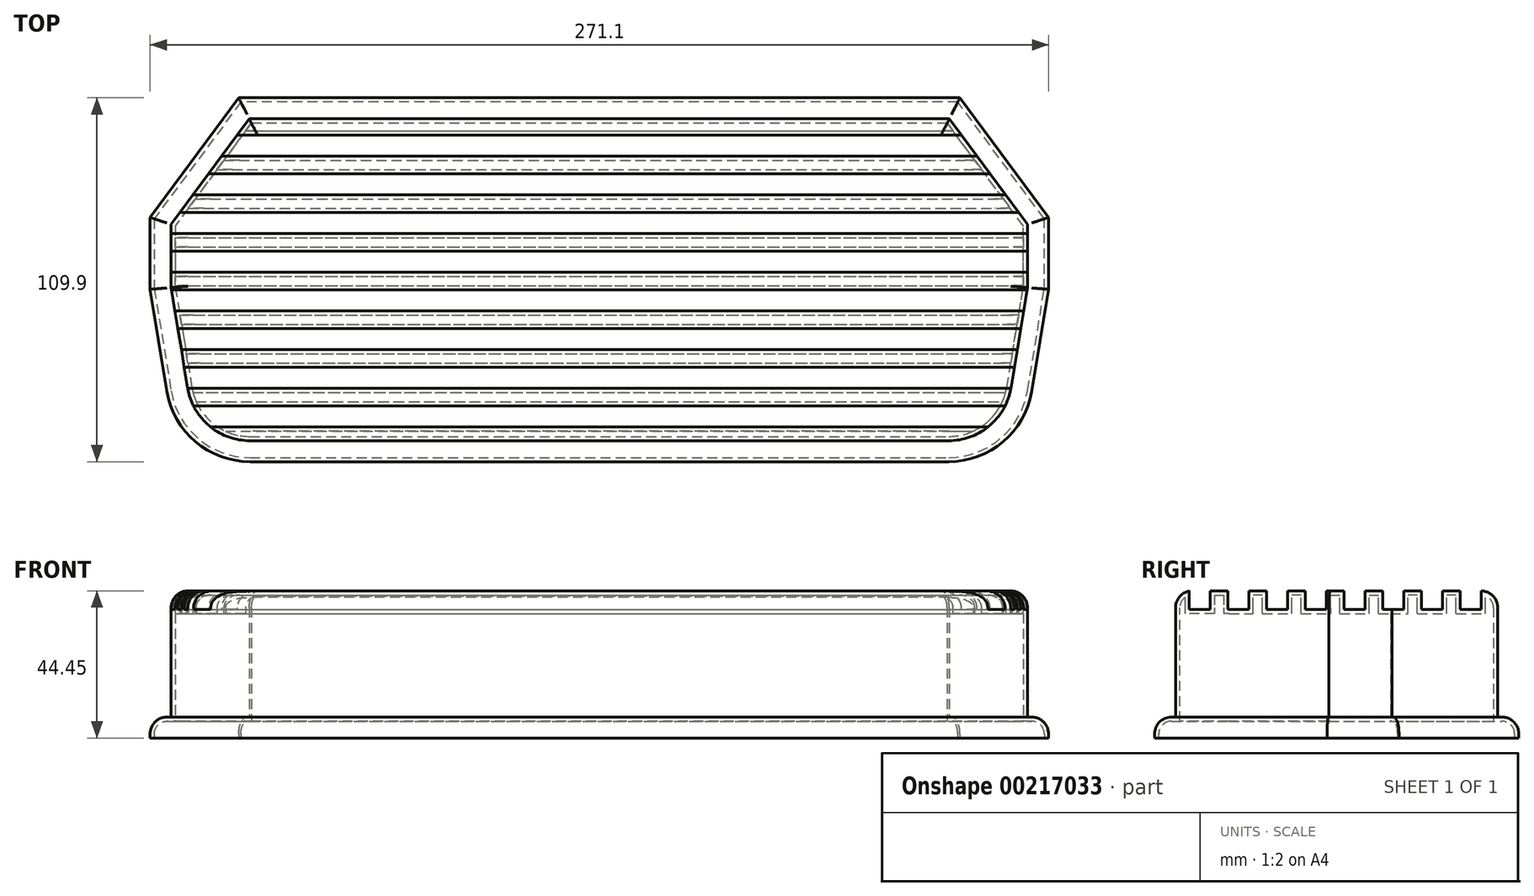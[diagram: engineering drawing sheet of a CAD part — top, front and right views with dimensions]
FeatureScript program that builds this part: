
annotation { "Feature Type Name" : "Feature", "Feature Type Description" : "" }
export const myFeature = defineFeature(function(context is Context, id is Id, definition is map)
    precondition{}
    {
        {
            var Q0;
            Q0=qCreatedBy(makeId("Top.planeOp"),FACE);
            var sketch = newSketch(context, id + "F0", { "sketchPlane" : qUnion([Q0])});
            skLineSegment(sketch, "E0.0.0", {"start": v(-203.12, -79.65) * mm, "end": v(7.7, -79.65) * mm});
            skArc(sketch, "E0.0.1", {"start": v(7.7, -79.65) * mm, "mid": v(20.03, -75.13) * mm, "end": v(26.5, -63.7) * mm});
            skLineSegment(sketch, "E0.0.2", {"start": v(26.5, -63.7) * mm, "end": v(31.49, -33.42) * mm});
            skLineSegment(sketch, "E0.0.3", {"start": v(31.49, -33.42) * mm, "end": v(31.49, -14.33) * mm});
            skLineSegment(sketch, "E0.0.4", {"start": v(31.49, -14.33) * mm, "end": v(7.9, 17.55) * mm});
            skLineSegment(sketch, "E0.0.5", {"start": v(7.9, 17.55) * mm, "end": v(-203.33, 17.55) * mm});
            skLineSegment(sketch, "E0.0.6", {"start": v(-203.33, 17.55) * mm, "end": v(-226.91, -14.33) * mm});
            skLineSegment(sketch, "E0.0.7", {"start": v(-226.91, -14.33) * mm, "end": v(-226.91, -33.42) * mm});
            skLineSegment(sketch, "E0.0.8", {"start": v(-226.91, -33.42) * mm, "end": v(-221.92, -63.7) * mm});
            skArc(sketch, "E0.0.9", {"start": v(-221.92, -63.7) * mm, "mid": v(-215.45, -75.13) * mm, "end": v(-203.12, -79.65) * mm});
            skArc(sketch, "E1.0", {"start": v(-228.19, -64.73) * mm, "mid": v(-219.56, -79.97) * mm, "end": v(-203.12, -86) * mm});
            skLineSegment(sketch, "E1.1", {"start": v(-233.26, -33.94) * mm, "end": v(-228.19, -64.73) * mm});
            skLineSegment(sketch, "E1.2", {"start": v(-203.12, -86) * mm, "end": v(7.7, -86) * mm});
            skLineSegment(sketch, "E1.3", {"start": v(-233.26, -12.24) * mm, "end": v(-233.26, -33.94) * mm});
            skLineSegment(sketch, "E1.4", {"start": v(-206.53, 23.9) * mm, "end": v(-233.26, -12.24) * mm});
            skLineSegment(sketch, "E1.5", {"start": v(11.1, 23.9) * mm, "end": v(-206.53, 23.9) * mm});
            skArc(sketch, "E1.6", {"start": v(7.7, -86) * mm, "mid": v(24.14, -79.97) * mm, "end": v(32.76, -64.73) * mm});
            skLineSegment(sketch, "E1.7", {"start": v(32.76, -64.73) * mm, "end": v(37.84, -33.94) * mm});
            skLineSegment(sketch, "E1.8", {"start": v(37.84, -33.94) * mm, "end": v(37.84, -12.24) * mm});
            skLineSegment(sketch, "E1.9", {"start": v(37.84, -12.24) * mm, "end": v(11.1, 23.9) * mm});
            skSolve(sketch);
        }
        {
            var Q0;
            Q0=makeQuery(id+"F0.imprint","IMPRINT",FACE,{"disambiguationData":[TD([[makeQuery(id+"F0.imprint","IMPRINT",EDGE,{"derivedFrom":sQuery(id+"F0.wireOp",EDGE,"E0.0.0")}),1.0]])]});
            extrude(context, id + "F1", {"entities" : qUnion([Q0]), "depth" : 44.45 * mm});
        }
        {
            var Q0;
            Q0=makeQuery(id+"F0.imprint","IMPRINT",FACE,{"disambiguationData":[TD([[makeQuery(id+"F0.imprint","IMPRINT",EDGE,{"derivedFrom":sQuery(id+"F0.wireOp",EDGE,"E0.0.0")}),-1.0]])]});
            extrude(context, id + "F2", {"entities" : qUnion([Q0]), "operationType" : NewBodyOperationType.ADD, "depth" : 6.35 * mm});
        }
        {
            var Q0;
            Q0=makeQuery(id+"F1.opExtrude","CAP_FACE",FACE,{"disambiguationData":[OSD([sQuery(id+"F0.wireOp",EDGE,"E0.0.0"),sQuery(id+"F0.wireOp",EDGE,"E0.0.1"),sQuery(id+"F0.wireOp",EDGE,"E0.0.2"),sQuery(id+"F0.wireOp",EDGE,"E0.0.3"),sQuery(id+"F0.wireOp",EDGE,"E0.0.4"),sQuery(id+"F0.wireOp",EDGE,"E0.0.5"),sQuery(id+"F0.wireOp",EDGE,"E0.0.6"),sQuery(id+"F0.wireOp",EDGE,"E0.0.7"),sQuery(id+"F0.wireOp",EDGE,"E0.0.8"),sQuery(id+"F0.wireOp",EDGE,"E0.0.9")])],"isStart":false});
            var Q1;
            Q1=makeQuery(id+"F2.opExtrude","CAP_EDGE",EDGE,{"disambiguationData":[OSD([sQuery(id+"F0.wireOp",EDGE,"E1.4")])],"isStart":false});
            var Q2;
            Q2=makeQuery(id+"F2.opExtrude","CAP_EDGE",EDGE,{"disambiguationData":[OSD([sQuery(id+"F0.wireOp",EDGE,"E1.3")])],"isStart":false});
            var Q3;
            Q3=makeQuery(id+"F2.opExtrude","CAP_EDGE",EDGE,{"disambiguationData":[OSD([sQuery(id+"F0.wireOp",EDGE,"E1.1")])],"isStart":false});
            var Q4;
            Q4=makeQuery(id+"F2.opExtrude","CAP_EDGE",EDGE,{"disambiguationData":[OSD([sQuery(id+"F0.wireOp",EDGE,"E1.5")])],"isStart":false});
            var Q5;
            Q5=makeQuery(id+"F2.opExtrude","CAP_EDGE",EDGE,{"disambiguationData":[OSD([sQuery(id+"F0.wireOp",EDGE,"E1.8")])],"isStart":false});
            var Q6;
            Q6=makeQuery(id+"F2.opExtrude","CAP_EDGE",EDGE,{"disambiguationData":[OSD([sQuery(id+"F0.wireOp",EDGE,"E1.9")])],"isStart":false});
            fillet(context, id + "F3", {"entities" : qUnion([Q0, Q1, Q2, Q3, Q4, Q5, Q6]), "radius" : 5.08 * mm, "tangentPropagation" : true, "allowEdgeOverflow" : false});
        }
        {
            var Q0;
            Q0=qCreatedBy(makeId("Right.planeOp"),FACE);
            var sketch = newSketch(context, id + "F4", { "sketchPlane" : qUnion([Q0])});
            skLineSegment(sketch, "E2.bottom", {"start": v(12.62, 51.56) * mm, "end": v(6.27, 51.56) * mm});
            skLineSegment(sketch, "E2.top", {"start": v(12.62, 38.86) * mm, "end": v(6.27, 38.86) * mm});
            skLineSegment(sketch, "E2.left", {"start": v(12.62, 51.56) * mm, "end": v(12.62, 38.86) * mm});
            skLineSegment(sketch, "E2.right", {"start": v(6.27, 51.56) * mm, "end": v(6.27, 38.86) * mm});
            skPoint(sketch, "E2.middle", {"position": v(9.45, 45.2) * mm});
            skLineSegment(sketch, "E3.1.0.0", {"start": v(-5.4, 51.56) * mm, "end": v(-5.4, 38.86) * mm});
            skLineSegment(sketch, "E3.1.0.1", {"start": v(0.94, 51.56) * mm, "end": v(-5.4, 51.56) * mm});
            skLineSegment(sketch, "E3.1.0.2", {"start": v(0.94, 51.56) * mm, "end": v(0.94, 38.86) * mm});
            skLineSegment(sketch, "E3.1.0.3", {"start": v(0.94, 38.86) * mm, "end": v(-5.4, 38.86) * mm});
            skLineSegment(sketch, "E3.2.0.0", {"start": v(-17.1, 51.56) * mm, "end": v(-17.1, 38.86) * mm});
            skLineSegment(sketch, "E3.2.0.1", {"start": v(-10.74, 51.56) * mm, "end": v(-17.1, 51.56) * mm});
            skLineSegment(sketch, "E3.2.0.2", {"start": v(-10.74, 51.56) * mm, "end": v(-10.74, 38.86) * mm});
            skLineSegment(sketch, "E3.2.0.3", {"start": v(-10.74, 38.86) * mm, "end": v(-17.1, 38.86) * mm});
            skLineSegment(sketch, "E3.3.0.0", {"start": v(-28.78, 51.56) * mm, "end": v(-28.78, 38.86) * mm});
            skLineSegment(sketch, "E3.3.0.1", {"start": v(-22.43, 51.56) * mm, "end": v(-28.78, 51.56) * mm});
            skLineSegment(sketch, "E3.3.0.2", {"start": v(-22.43, 51.56) * mm, "end": v(-22.43, 38.86) * mm});
            skLineSegment(sketch, "E3.3.0.3", {"start": v(-22.43, 38.86) * mm, "end": v(-28.78, 38.86) * mm});
            skLineSegment(sketch, "E3.4.0.0", {"start": v(-40.46, 51.56) * mm, "end": v(-40.46, 38.86) * mm});
            skLineSegment(sketch, "E3.4.0.1", {"start": v(-34.11, 51.56) * mm, "end": v(-40.46, 51.56) * mm});
            skLineSegment(sketch, "E3.4.0.2", {"start": v(-34.11, 51.56) * mm, "end": v(-34.11, 38.86) * mm});
            skLineSegment(sketch, "E3.4.0.3", {"start": v(-34.11, 38.86) * mm, "end": v(-40.46, 38.86) * mm});
            skLineSegment(sketch, "E3.5.0.0", {"start": v(-52.15, 51.56) * mm, "end": v(-52.15, 38.86) * mm});
            skLineSegment(sketch, "E3.5.0.1", {"start": v(-45.8, 51.56) * mm, "end": v(-52.15, 51.56) * mm});
            skLineSegment(sketch, "E3.5.0.2", {"start": v(-45.8, 51.56) * mm, "end": v(-45.8, 38.86) * mm});
            skLineSegment(sketch, "E3.5.0.3", {"start": v(-45.8, 38.86) * mm, "end": v(-52.15, 38.86) * mm});
            skLineSegment(sketch, "E3.6.0.0", {"start": v(-63.83, 51.56) * mm, "end": v(-63.83, 38.86) * mm});
            skLineSegment(sketch, "E3.6.0.1", {"start": v(-57.48, 51.56) * mm, "end": v(-63.83, 51.56) * mm});
            skLineSegment(sketch, "E3.6.0.2", {"start": v(-57.48, 51.56) * mm, "end": v(-57.48, 38.86) * mm});
            skLineSegment(sketch, "E3.6.0.3", {"start": v(-57.48, 38.86) * mm, "end": v(-63.83, 38.86) * mm});
            skLineSegment(sketch, "E3.7.0.0", {"start": v(-75.51, 51.56) * mm, "end": v(-75.51, 38.86) * mm});
            skLineSegment(sketch, "E3.7.0.1", {"start": v(-69.16, 51.56) * mm, "end": v(-75.51, 51.56) * mm});
            skLineSegment(sketch, "E3.7.0.2", {"start": v(-69.16, 51.56) * mm, "end": v(-69.16, 38.86) * mm});
            skLineSegment(sketch, "E3.7.0.3", {"start": v(-69.16, 38.86) * mm, "end": v(-75.51, 38.86) * mm});
            skLineSegment(sketch, "E3.direction1", {"start": v(6.27, 38.86) * mm, "end": v(-5.4, 38.86) * mm, "construction": true});
            skSolve(sketch);
        }
        {
            var Q0;
            Q0=makeQuery(id+"F4.imprint","IMPRINT",FACE,{"disambiguationData":[TD([[makeQuery(id+"F4.imprint","IMPRINT",EDGE,{"derivedFrom":sQuery(id+"F4.wireOp",EDGE,"E2.bottom")}),1.0]])]});
            var Q1;
            Q1=makeQuery(id+"F4.imprint","IMPRINT",FACE,{"disambiguationData":[TD([[makeQuery(id+"F4.imprint","IMPRINT",EDGE,{"derivedFrom":sQuery(id+"F4.wireOp",EDGE,"E3.1.0.0")}),1.0]])]});
            var Q2;
            Q2=makeQuery(id+"F4.imprint","IMPRINT",FACE,{"disambiguationData":[TD([[makeQuery(id+"F4.imprint","IMPRINT",EDGE,{"derivedFrom":sQuery(id+"F4.wireOp",EDGE,"E3.2.0.0")}),1.0]])]});
            var Q3;
            Q3=makeQuery(id+"F4.imprint","IMPRINT",FACE,{"disambiguationData":[TD([[makeQuery(id+"F4.imprint","IMPRINT",EDGE,{"derivedFrom":sQuery(id+"F4.wireOp",EDGE,"E3.3.0.0")}),1.0]])]});
            var Q4;
            Q4=makeQuery(id+"F4.imprint","IMPRINT",FACE,{"disambiguationData":[TD([[makeQuery(id+"F4.imprint","IMPRINT",EDGE,{"derivedFrom":sQuery(id+"F4.wireOp",EDGE,"E3.4.0.0")}),1.0]])]});
            var Q5;
            Q5=makeQuery(id+"F4.imprint","IMPRINT",FACE,{"disambiguationData":[TD([[makeQuery(id+"F4.imprint","IMPRINT",EDGE,{"derivedFrom":sQuery(id+"F4.wireOp",EDGE,"E3.5.0.0")}),1.0]])]});
            var Q6;
            Q6=makeQuery(id+"F4.imprint","IMPRINT",FACE,{"disambiguationData":[TD([[makeQuery(id+"F4.imprint","IMPRINT",EDGE,{"derivedFrom":sQuery(id+"F4.wireOp",EDGE,"E3.6.0.0")}),1.0]])]});
            var Q7;
            Q7=makeQuery(id+"F4.imprint","IMPRINT",FACE,{"disambiguationData":[TD([[makeQuery(id+"F4.imprint","IMPRINT",EDGE,{"derivedFrom":sQuery(id+"F4.wireOp",EDGE,"E3.7.0.0")}),1.0]])]});
            extrude(context, id + "F5", {"entities" : qUnion([Q0, Q1, Q2, Q3, Q4, Q5, Q6, Q7]), "operationType" : NewBodyOperationType.REMOVE, "oppositeDirection" : true, "depth" : 762 * mm, "symmetric" : true});
        }
        {
            var Q0;
            {var subQ0=sQuery(id+"F0.wireOp",EDGE,"E0.0.9");var subQ1=sQuery(id+"F0.wireOp",EDGE,"E0.0.8");var subQ2=sQuery(id+"F0.wireOp",EDGE,"E0.0.7");var subQ3=sQuery(id+"F0.wireOp",EDGE,"E0.0.6");var subQ4=sQuery(id+"F0.wireOp",EDGE,"E0.0.5");var subQ5=sQuery(id+"F0.wireOp",EDGE,"E0.0.4");var subQ6=sQuery(id+"F0.wireOp",EDGE,"E0.0.3");var subQ7=sQuery(id+"F0.wireOp",EDGE,"E0.0.2");var subQ8=sQuery(id+"F0.wireOp",EDGE,"E0.0.1");var subQ9=sQuery(id+"F0.wireOp",EDGE,"E0.0.0");Q0=makeQuery(id+"F2.boolean.opBoolean","MERGE",FACE,{"derivedFrom":[makeQuery(id+"F1.opExtrude","CAP_FACE",FACE,{"disambiguationData":[OSD([subQ9,subQ8,subQ7,subQ6,subQ5,subQ4,subQ3,subQ2,subQ1,subQ0])],"isStart":true}),makeQuery(id+"F2.opExtrude","CAP_FACE",FACE,{"disambiguationData":[OSD([subQ9,subQ8,subQ7,subQ6,subQ5,subQ4,subQ3,subQ2,subQ1,subQ0,sQuery(id+"F0.wireOp",EDGE,"E1.0"),sQuery(id+"F0.wireOp",EDGE,"E1.1"),sQuery(id+"F0.wireOp",EDGE,"E1.2"),sQuery(id+"F0.wireOp",EDGE,"E1.3"),sQuery(id+"F0.wireOp",EDGE,"E1.4"),sQuery(id+"F0.wireOp",EDGE,"E1.5"),sQuery(id+"F0.wireOp",EDGE,"E1.6"),sQuery(id+"F0.wireOp",EDGE,"E1.7"),sQuery(id+"F0.wireOp",EDGE,"E1.8"),sQuery(id+"F0.wireOp",EDGE,"E1.9")])],"isStart":true})]});}
            shell(context, id + "F6", {"entities" : qUnion([Q0]), "thickness" : 1.27 * mm});
        }
    });
